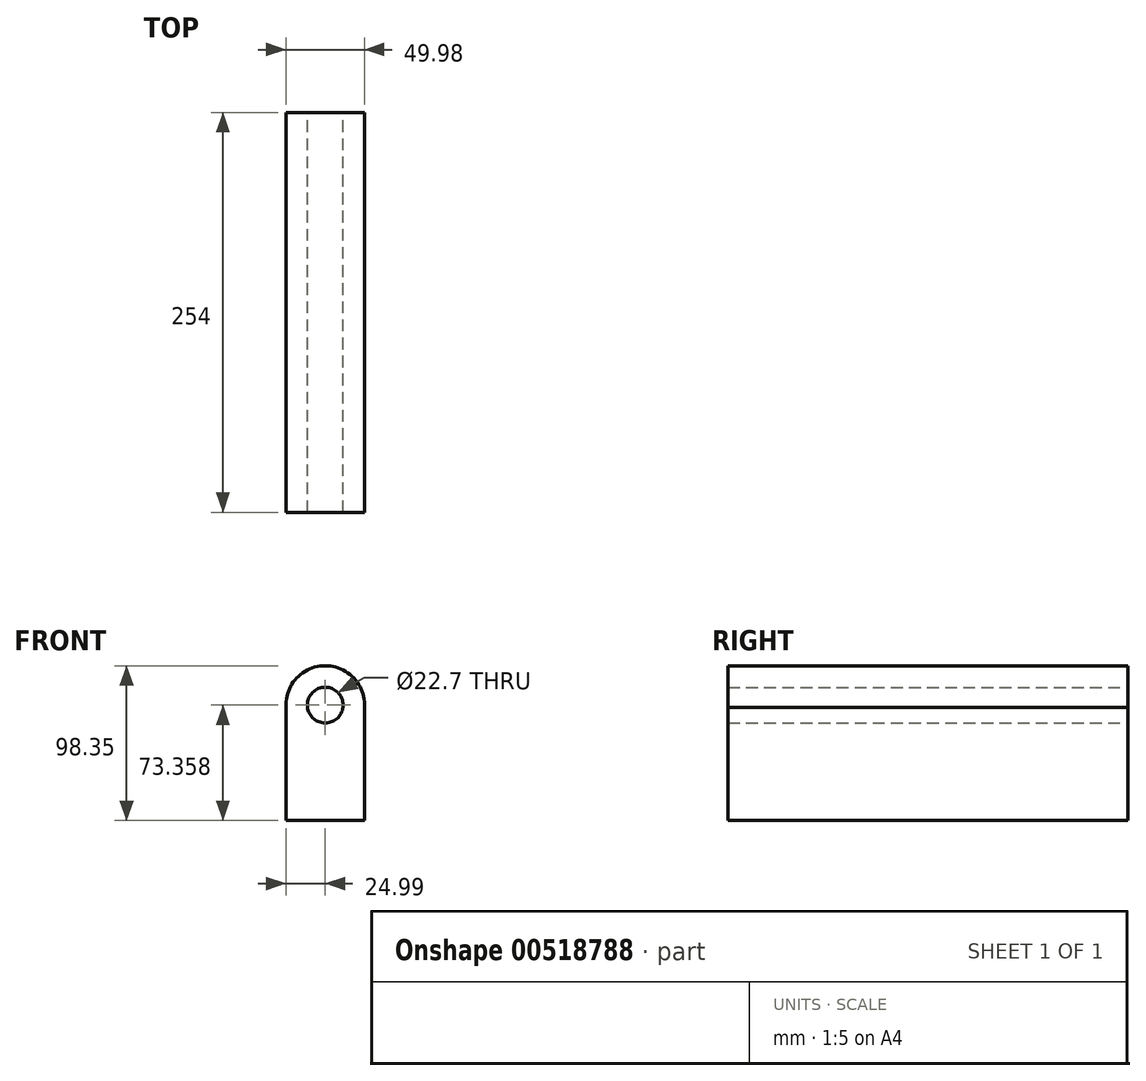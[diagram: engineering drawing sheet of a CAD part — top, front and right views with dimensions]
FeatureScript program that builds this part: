
annotation { "Feature Type Name" : "Feature", "Feature Type Description" : "" }
export const myFeature = defineFeature(function(context is Context, id is Id, definition is map)
    precondition{}
    {
        {
            var Q0;
            Q0=qCreatedBy(makeId("Front.planeOp"),FACE);
            var sketch = newSketch(context, id + "F0", { "sketchPlane" : qUnion([Q0])});
            skLineSegment(sketch, "E0.bottom", {"start": v(-25.78, 31.64) * mm, "end": v(24.14, 31.64) * mm});
            skLineSegment(sketch, "E0.top", {"start": v(-25.78, -41.72) * mm, "end": v(24.14, -41.72) * mm});
            skLineSegment(sketch, "E0.left", {"start": v(-25.78, 31.64) * mm, "end": v(-25.78, -41.72) * mm});
            skLineSegment(sketch, "E0.right", {"start": v(24.14, 31.64) * mm, "end": v(24.14, -41.72) * mm});
            skCircle(sketch, "E1", {"center": v(-0.82, 31.64) * mm, "radius": 25 * mm});
            skCircle(sketch, "E2", {"center": v(-0.82, 31.64) * mm, "radius": 11.35 * mm});
            skSolve(sketch);
        }
        {
            var Q0;
            Q0 = qSketchRegion(id + "F0", true);
            extrude(context, id + "F1", {"entities" : qUnion([Q0]), "depth" : 254 * mm});
        }
    });
